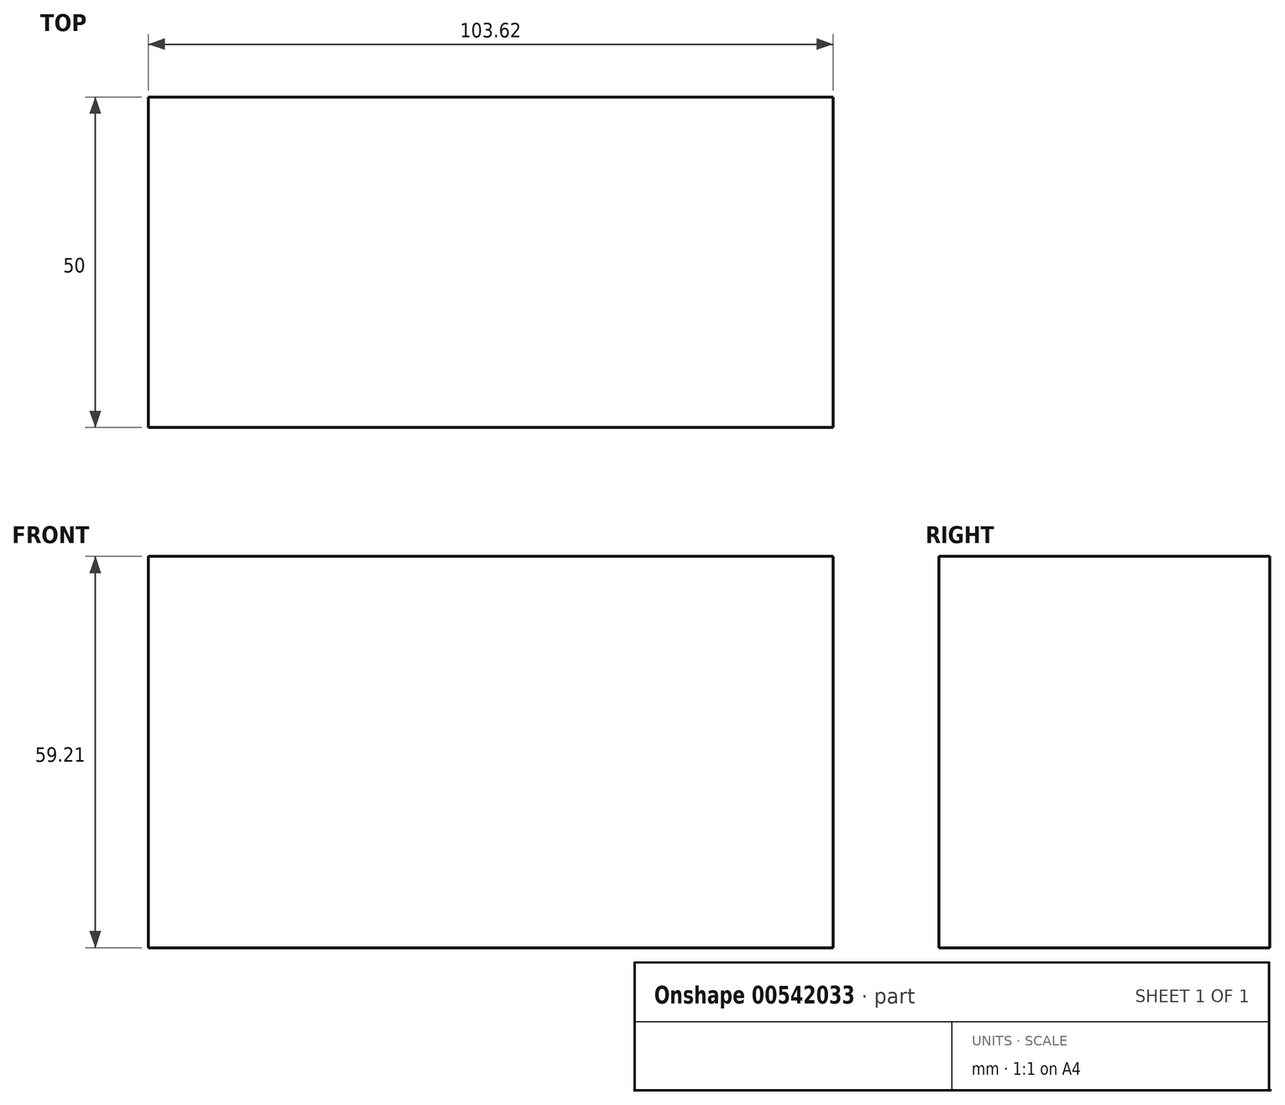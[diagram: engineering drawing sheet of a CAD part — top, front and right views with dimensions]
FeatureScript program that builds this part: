
annotation { "Feature Type Name" : "Feature", "Feature Type Description" : "" }
export const myFeature = defineFeature(function(context is Context, id is Id, definition is map)
    precondition{}
    {
        {
            var Q0;
            Q0=qCreatedBy(makeId("Front.planeOp"),FACE);
            var sketch = newSketch(context, id + "F0", { "sketchPlane" : qUnion([Q0])});
            skLineSegment(sketch, "E0.bottom", {"start": v(-50.92, 28.42) * mm, "end": v(52.7, 28.42) * mm});
            skLineSegment(sketch, "E0.top", {"start": v(-50.92, -30.79) * mm, "end": v(52.7, -30.79) * mm});
            skLineSegment(sketch, "E0.left", {"start": v(-50.92, 28.42) * mm, "end": v(-50.92, -30.79) * mm});
            skLineSegment(sketch, "E0.right", {"start": v(52.7, 28.42) * mm, "end": v(52.7, -30.79) * mm});
            skSolve(sketch);
        }
        {
            var Q0;
            Q0=makeQuery(id+"F0.imprint","IMPRINT",FACE,{"disambiguationData":[TD([[makeQuery(id+"F0.imprint","IMPRINT",EDGE,{"derivedFrom":sQuery(id+"F0.wireOp",EDGE,"E0.bottom")}),-1.0]])]});
            extrude(context, id + "F1", {"entities" : qUnion([Q0]), "depth" : 50 * mm, "offsetDistance" : 25 * mm, "hasDraft" : true, "draftAngle" : 0 * degree});
        }
    });
